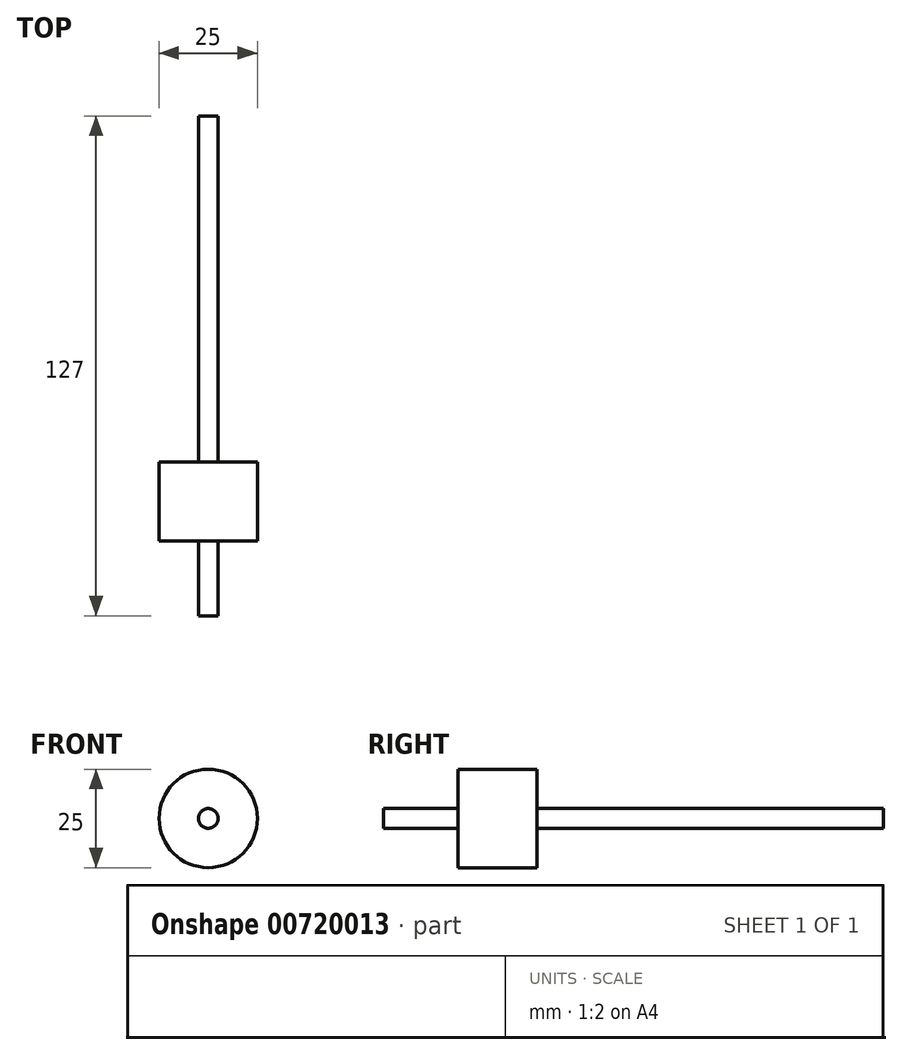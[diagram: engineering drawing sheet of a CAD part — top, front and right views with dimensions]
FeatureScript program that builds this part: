
annotation { "Feature Type Name" : "Feature", "Feature Type Description" : "" }
export const myFeature = defineFeature(function(context is Context, id is Id, definition is map)
    precondition{}
    {
        {
            var Q0;
            Q0=qCreatedBy(makeId("Front.planeOp"),FACE);
            var sketch = newSketch(context, id + "F0", { "sketchPlane" : qUnion([Q0])});
            skCircle(sketch, "E0", {"center": v(0, 0) * mm, "radius": 12.5 * mm});
            skCircle(sketch, "E1", {"center": v(0, 0) * mm, "radius": 2.5 * mm});
            skSolve(sketch);
        }
        {
            var Q0;
            Q0=makeQuery(id+"F0.imprint","IMPRINT",FACE,{"disambiguationData":[TD([[makeQuery(id+"F0.imprint","IMPRINT",EDGE,{"derivedFrom":sQuery(id+"F0.wireOp",EDGE,"E1")}),1.0]])]});
            extrude(context, id + "F1", {"entities" : qUnion([Q0]), "depth" : 39 * mm, "offsetDistance" : 25 * mm});
        }
        {
            var Q0;
            Q0 = qSketchRegion(id + "F0", true);
            extrude(context, id + "F2", {"entities" : qUnion([Q0]), "operationType" : NewBodyOperationType.ADD, "depth" : 20 * mm, "offsetDistance" : 25 * mm});
        }
        {
            var Q0;
            Q0=makeQuery(id+"F0.imprint","IMPRINT",FACE,{"disambiguationData":[TD([[makeQuery(id+"F0.imprint","IMPRINT",EDGE,{"derivedFrom":sQuery(id+"F0.wireOp",EDGE,"E1")}),1.0]])]});
            extrude(context, id + "F3", {"entities" : qUnion([Q0]), "operationType" : NewBodyOperationType.ADD, "oppositeDirection" : true, "depth" : 88 * mm, "offsetDistance" : 25 * mm});
        }
    });
